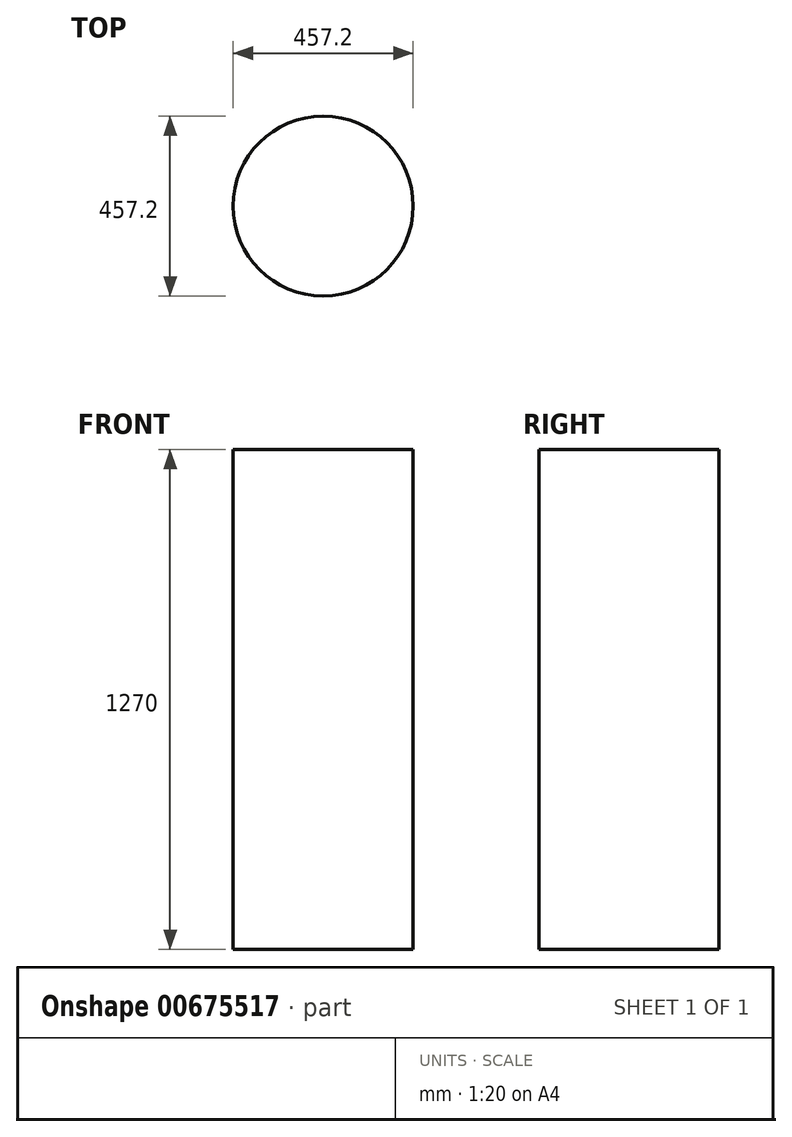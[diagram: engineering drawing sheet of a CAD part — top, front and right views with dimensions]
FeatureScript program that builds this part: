
annotation { "Feature Type Name" : "Feature", "Feature Type Description" : "" }
export const myFeature = defineFeature(function(context is Context, id is Id, definition is map)
    precondition{}
    {
        {
            var Q0;
            Q0=qCreatedBy(makeId("Top.planeOp"),FACE);
            var sketch = newSketch(context, id + "F0", { "sketchPlane" : qUnion([Q0])});
            skCircle(sketch, "E0", {"center": v(0, 0) * mm, "radius": 228.6 * mm});
            skSolve(sketch);
        }
        {
            var Q0;
            Q0 = qSketchRegion(id + "F0", true);
            extrude(context, id + "F1", {"entities" : qUnion([Q0]), "depth" : 1270 * mm, "offsetDistance" : 25.4 * mm});
        }
    });
